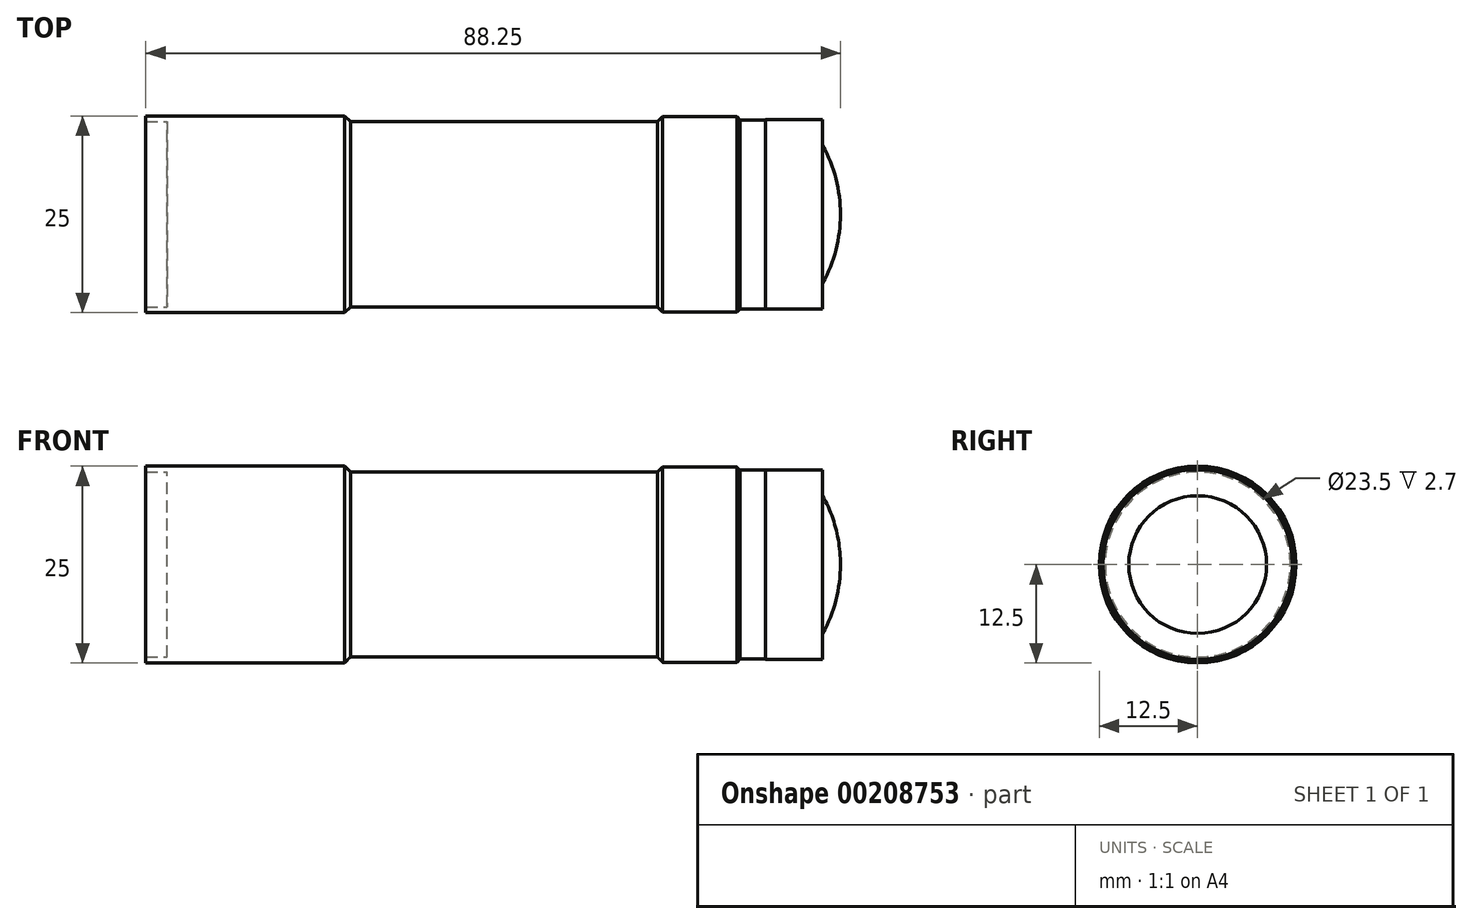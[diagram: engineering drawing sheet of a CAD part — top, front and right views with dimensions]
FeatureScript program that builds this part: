
annotation { "Feature Type Name" : "Feature", "Feature Type Description" : "" }
export const myFeature = defineFeature(function(context is Context, id is Id, definition is map)
    precondition{}
    {
        {
            var Q0;
            Q0=qCreatedBy(makeId("Front.planeOp"),FACE);
            var sketch = newSketch(context, id + "F0", { "sketchPlane" : qUnion([Q0])});
            skLineSegment(sketch, "E0", {"start": v(-85.55, 0) * mm, "end": v(-85.55, 11.75) * mm});
            skLineSegment(sketch, "E1", {"start": v(-85.55, 11.75) * mm, "end": v(-88.25, 11.75) * mm});
            skLineSegment(sketch, "E2", {"start": v(-88.25, 11.75) * mm, "end": v(-88.25, 12.5) * mm});
            skLineSegment(sketch, "E3", {"start": v(-88.25, 12.5) * mm, "end": v(-62.25, 12.5) * mm});
            skLineSegment(sketch, "E4", {"start": v(-62.25, 12.5) * mm, "end": v(-62.25, 11.75) * mm});
            skLineSegment(sketch, "E5", {"start": v(-62.25, 11.75) * mm, "end": v(-23.25, 11.75) * mm});
            skLineSegment(sketch, "E6", {"start": v(-23.25, 12.4) * mm, "end": v(-12.75, 12.4) * mm});
            skLineSegment(sketch, "E7", {"start": v(-12.75, 12.4) * mm, "end": v(-12.75, 12) * mm});
            skLineSegment(sketch, "E8", {"start": v(-12.75, 12) * mm, "end": v(-9.5, 12) * mm});
            skLineSegment(sketch, "E9", {"start": v(-9.5, 12) * mm, "end": v(-9.5, 12.05) * mm});
            skLineSegment(sketch, "E10", {"start": v(-9.5, 12.05) * mm, "end": v(-2.25, 12.05) * mm});
            skLineSegment(sketch, "E11", {"start": v(-2.25, 12.05) * mm, "end": v(-2.25, 8.75) * mm});
            skArc(sketch, "E12", {"start": v(-2.25, 8.75) * mm, "mid": v(-0.57, 4.52) * mm, "end": v(0, 0) * mm});
            skLineSegment(sketch, "E13", {"start": v(-23.25, 12.4) * mm, "end": v(-23.25, 11.75) * mm});
            skPoint(sketch, "E14.start.orphan", {"position": v(0, 0) * mm});
            skLineSegment(sketch, "E15", {"start": v(0, 0) * mm, "end": v(-92.72, 0) * mm, "construction": true});
            skLineSegment(sketch, "E16", {"start": v(0, 0) * mm, "end": v(-85.55, 0) * mm});
            skSolve(sketch);
        }
        {
            var Q0;
            Q0=makeQuery(id+"F0.imprint","IMPRINT",FACE,{"disambiguationData":[TD([[makeQuery(id+"F0.imprint","IMPRINT",EDGE,{"derivedFrom":sQuery(id+"F0.wireOp",EDGE,"E0")}),-1.0]])]});
            var Q1;
            Q1=sQuery(id+"F0.wireOp",EDGE,"E15");
            revolve(context, id + "F1", {"entities" : qUnion([Q0]), "axis" : qUnion([Q1]), "revolveType" : RevolveType.FULL});
        }
        {
            var Q0;
            Q0=makeQuery(id+"F1.opRevolve","SWEPT_EDGE",EDGE,{"disambiguationData":[OSD([sQuery(id+"F0.wireOp",EDGE,"E3"),sQuery(id+"F0.wireOp",EDGE,"E4")])]});
            chamfer(context, id + "F2", {"entities" : qUnion([Q0]), "width" : .75 * mm, "tangentPropagation" : true});
        }
        {
            var Q0;
            Q0=makeQuery(id+"F1.opRevolve","SWEPT_EDGE",EDGE,{"disambiguationData":[OSD([sQuery(id+"F0.wireOp",EDGE,"E6"),sQuery(id+"F0.wireOp",EDGE,"E13")])]});
            chamfer(context, id + "F3", {"entities" : qUnion([Q0]), "width" : .65 * mm, "tangentPropagation" : true});
        }
        {
            var Q0;
            Q0=makeQuery(id+"F1.opRevolve","SWEPT_EDGE",EDGE,{"disambiguationData":[OSD([sQuery(id+"F0.wireOp",EDGE,"E6"),sQuery(id+"F0.wireOp",EDGE,"E7")])]});
            chamfer(context, id + "F4", {"entities" : qUnion([Q0]), "width" : .4 * mm, "tangentPropagation" : true});
        }
    });
